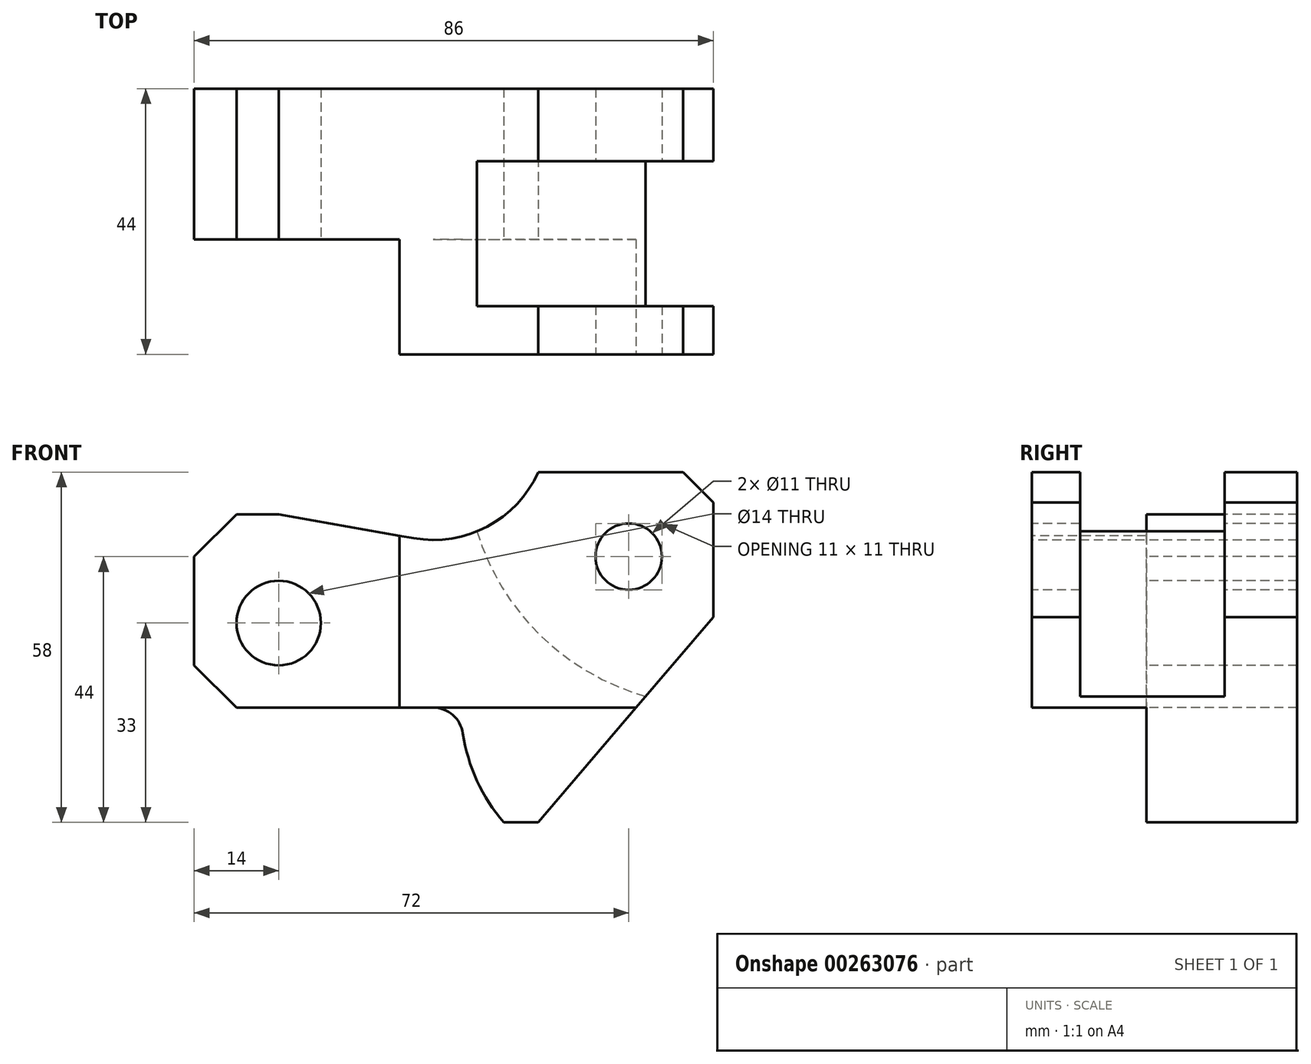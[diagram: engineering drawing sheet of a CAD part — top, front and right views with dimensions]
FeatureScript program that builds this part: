
annotation { "Feature Type Name" : "Feature", "Feature Type Description" : "" }
export const myFeature = defineFeature(function(context is Context, id is Id, definition is map)
    precondition{}
    {
        {
            var Q0;
            Q0=qCreatedBy(makeId("Front.planeOp"),FACE);
            var sketch = newSketch(context, id + "F0", { "sketchPlane" : qUnion([Q0])});
            skCircle(sketch, "E0", {"center": v(0, 0) * mm, "radius": 7 * mm});
            skLineSegment(sketch, "E1", {"start": v(-14, -7) * mm, "end": v(-14, 11) * mm});
            skLineSegment(sketch, "E2", {"start": v(-14, 11) * mm, "end": v(-7, 18) * mm});
            skLineSegment(sketch, "E3", {"start": v(-7, 18) * mm, "end": v(0, 18) * mm});
            skLineSegment(sketch, "E4", {"start": v(0, 18) * mm, "end": v(22.36, 14.06) * mm});
            skArc(sketch, "E5", {"start": v(22.36, 14.06) * mm, "mid": v(34.56, 15.98) * mm, "end": v(43, 25) * mm});
            skLineSegment(sketch, "E6", {"start": v(43, 25) * mm, "end": v(67, 25) * mm});
            skLineSegment(sketch, "E7", {"start": v(67, 25) * mm, "end": v(72, 20) * mm});
            skLineSegment(sketch, "E8", {"start": v(72, 20) * mm, "end": v(72, 1) * mm});
            skLineSegment(sketch, "E9", {"start": v(72, 1) * mm, "end": v(43, -33) * mm});
            skLineSegment(sketch, "E10", {"start": v(43, -33) * mm, "end": v(37.3, -33) * mm});
            skLineSegment(sketch, "E11", {"start": v(-7, -14) * mm, "end": v(-14, -7) * mm});
            skArc(sketch, "E12", {"start": v(30.52, -18.26) * mm, "mid": v(32.86, -26.12) * mm, "end": v(37.3, -33) * mm});
            skArc(sketch, "E13", {"start": v(30.52, -18.26) * mm, "mid": v(28.84, -15.21) * mm, "end": v(25.58, -14) * mm});
            skLineSegment(sketch, "E14", {"start": v(-7, -14) * mm, "end": v(25.58, -14) * mm});
            skLineSegment(sketch, "E15", {"start": v(20, 14.47) * mm, "end": v(20, -14) * mm});
            skCircle(sketch, "E16", {"center": v(58, 11) * mm, "radius": 5.5 * mm});
            skLineSegment(sketch, "E17", {"start": v(25.58, -14) * mm, "end": v(59.2, -14) * mm});
            skLineSegment(sketch, "E18", {"start": v(72, 1) * mm, "end": v(59.2, -14) * mm});
            skLineSegment(sketch, "E19", {"start": v(25.58, -14) * mm, "end": v(20, -14) * mm});
            skLineSegment(sketch, "E20", {"start": v(20, 14.47) * mm, "end": v(22.36, 14.06) * mm});
            skLineSegment(sketch, "E21", {"start": v(20, -14) * mm, "end": v(59.2, -14) * mm});
            skSolve(sketch);
        }
        {
            var Q0;
            Q0 = qSketchRegion(id + "F0", true);
            extrude(context, id + "F1", {"entities" : qUnion([Q0]), "oppositeDirection" : true, "depth" : 44 * mm});
        }
        {
            var Q0;
            Q0=makeQuery(id+"F0.imprint","IMPRINT",FACE,{"disambiguationData":[TD([[makeQuery(id+"F0.imprint","IMPRINT",EDGE,{"derivedFrom":sQuery(id+"F0.wireOp",EDGE,"E0")}),-1.0]])]});
            extrude(context, id + "F2", {"entities" : qUnion([Q0]), "operationType" : NewBodyOperationType.REMOVE, "oppositeDirection" : true, "depth" : 19 * mm});
        }
        {
            var Q0;
            Q0=makeQuery(id+"F1.opExtrude","CAP_FACE",FACE,{"disambiguationData":[OSD([sQuery(id+"F0.wireOp",EDGE,"E0"),sQuery(id+"F0.wireOp",EDGE,"E1"),sQuery(id+"F0.wireOp",EDGE,"E2"),sQuery(id+"F0.wireOp",EDGE,"E3"),sQuery(id+"F0.wireOp",EDGE,"E4"),sQuery(id+"F0.wireOp",EDGE,"E5"),sQuery(id+"F0.wireOp",EDGE,"E6"),sQuery(id+"F0.wireOp",EDGE,"E7"),sQuery(id+"F0.wireOp",EDGE,"E8"),sQuery(id+"F0.wireOp",EDGE,"E9"),sQuery(id+"F0.wireOp",EDGE,"E10"),sQuery(id+"F0.wireOp",EDGE,"E11"),sQuery(id+"F0.wireOp",EDGE,"E12"),sQuery(id+"F0.wireOp",EDGE,"E13"),sQuery(id+"F0.wireOp",EDGE,"E14"),sQuery(id+"F0.wireOp",EDGE,"E16")])],"isStart":false});
            cPlane(context, id + "F3", {"entities" : qUnion([Q0]), "cplaneType" : CPlaneType.OFFSET, "offset" : 12 * mm, "oppositeDirection" : true, "width" : 150 * mm, "height" : 150 * mm});
        }
        {
            var Q0;
            Q0=qCreatedBy(id+"F3.planeOp",FACE);
            var sketch = newSketch(context, id + "F4", { "sketchPlane" : qUnion([Q0])});
            skArc(sketch, "E22", {"start": v(-79.1, -13.08) * mm, "mid": v(-39.79, 1.94) * mm, "end": v(-34.4, 43.67) * mm});
            skLineSegment(sketch, "E23", {"start": v(-79.1, -13.08) * mm, "end": v(-79.1, 42.85) * mm});
            skLineSegment(sketch, "E24", {"start": v(-79.1, 42.85) * mm, "end": v(-34.4, 43.67) * mm});
            skSolve(sketch);
        }
        {
            var Q0;
            Q0 = qSketchRegion(id + "F4", true);
            extrude(context, id + "F5", {"entities" : qUnion([Q0]), "operationType" : NewBodyOperationType.REMOVE, "oppositeDirection" : true, "depth" : 24 * mm});
        }
        {
            var Q0;
            {var subQ0=sQuery(id+"F0.wireOp",EDGE,"E10");Q0=makeQuery(id+"F0.imprint","IMPRINT",FACE,{"disambiguationData":[TD([[makeQuery(id+"F0.imprint","IMPRINT",EDGE,{"derivedFrom":subQ0}),-1.0]])]});}
            extrude(context, id + "F6", {"entities" : qUnion([Q0]), "operationType" : NewBodyOperationType.REMOVE, "oppositeDirection" : true, "depth" : 19 * mm});
        }
    });
